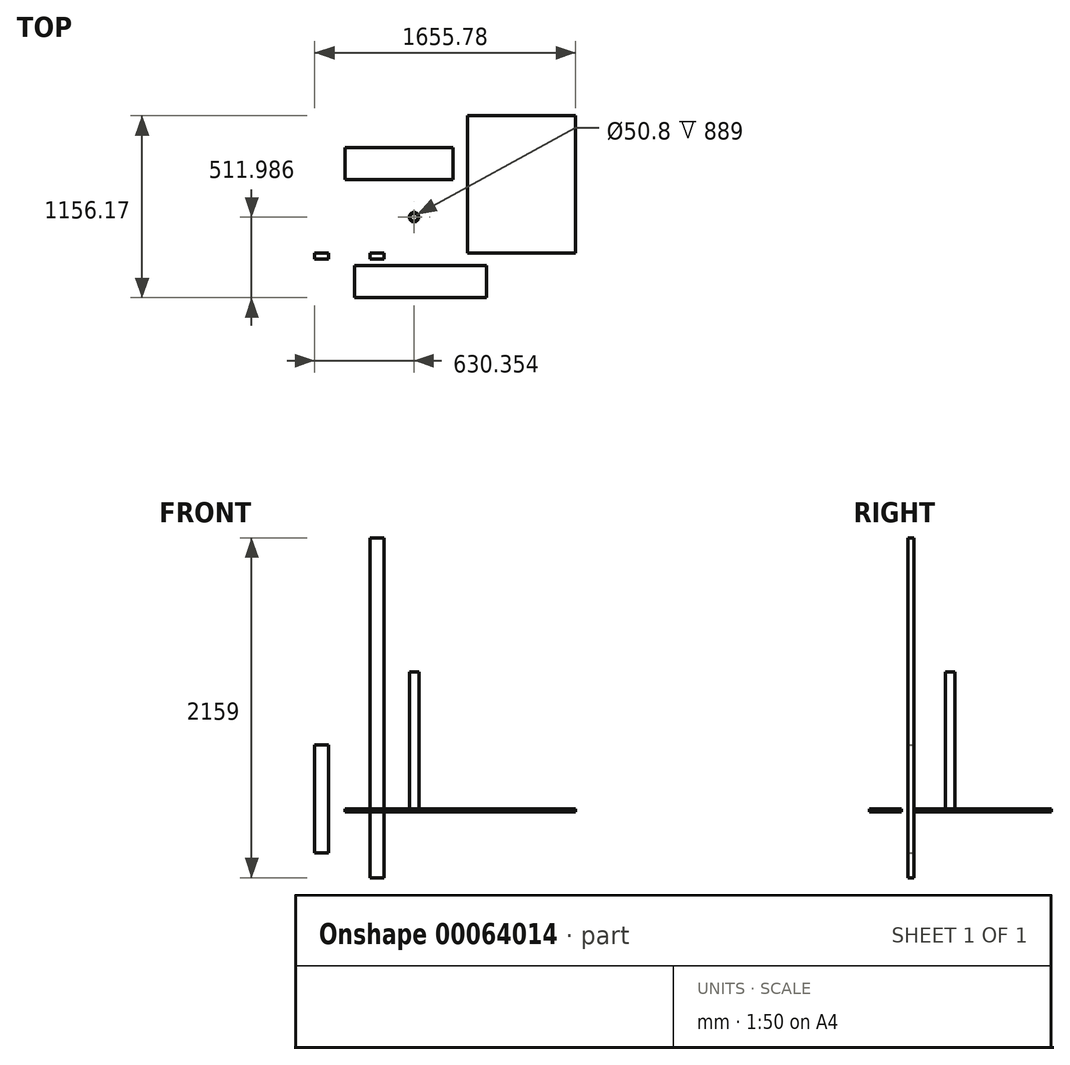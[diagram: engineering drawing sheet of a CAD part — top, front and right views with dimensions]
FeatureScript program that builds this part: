
annotation { "Feature Type Name" : "Feature", "Feature Type Description" : "" }
export const myFeature = defineFeature(function(context is Context, id is Id, definition is map)
    precondition{}
    {
        {
            var Q0;
            Q0=qCreatedBy(makeId("Front.planeOp"),FACE);
            var sketch = newSketch(context, id + "F0", { "sketchPlane" : qUnion([Q0])});
            skLineSegment(sketch, "E0.bottom", {"start": v(-46.7, 1742.14) * mm, "end": v(42.2, 1742.14) * mm});
            skLineSegment(sketch, "E0.top", {"start": v(-46.7, -416.86) * mm, "end": v(42.2, -416.86) * mm});
            skLineSegment(sketch, "E0.left", {"start": v(-46.7, 1742.14) * mm, "end": v(-46.7, -416.86) * mm});
            skLineSegment(sketch, "E0.right", {"start": v(42.2, 1742.14) * mm, "end": v(42.2, -416.86) * mm});
            skSolve(sketch);
        }
        {
            var Q0;
            Q0 = qSketchRegion(id + "F0", true);
            extrude(context, id + "F1", {"entities" : qUnion([Q0]), "depth" : 38.1 * mm});
        }
        {
            var Q0;
            Q0=qCreatedBy(makeId("Front.planeOp"),FACE);
            var sketch = newSketch(context, id + "F2", { "sketchPlane" : qUnion([Q0])});
            skLineSegment(sketch, "E1.bottom", {"start": v(-397.5, 426.42) * mm, "end": v(-308.6, 426.42) * mm});
            skLineSegment(sketch, "E1.top", {"start": v(-397.5, -259.38) * mm, "end": v(-308.6, -259.38) * mm});
            skLineSegment(sketch, "E1.left", {"start": v(-397.5, 426.42) * mm, "end": v(-397.5, -259.38) * mm});
            skLineSegment(sketch, "E1.right", {"start": v(-308.6, 426.42) * mm, "end": v(-308.6, -259.38) * mm});
            skSolve(sketch);
        }
        {
            var Q0;
            Q0 = qSketchRegion(id + "F2", true);
            extrude(context, id + "F3", {"entities" : qUnion([Q0]), "depth" : 38.1 * mm});
        }
        {
            var Q0;
            Q0=qCreatedBy(makeId("Top.planeOp"),FACE);
            var sketch = newSketch(context, id + "F4", { "sketchPlane" : qUnion([Q0])});
            skLineSegment(sketch, "E2.bottom", {"start": v(572.5, 0) * mm, "end": v(1258.3, 0) * mm});
            skLineSegment(sketch, "E2.top", {"start": v(572.5, 873.76) * mm, "end": v(1258.3, 873.76) * mm});
            skLineSegment(sketch, "E2.left", {"start": v(572.5, 0) * mm, "end": v(572.5, 873.76) * mm});
            skLineSegment(sketch, "E2.right", {"start": v(1258.3, 0) * mm, "end": v(1258.3, 873.76) * mm});
            skSolve(sketch);
        }
        {
            var Q0;
            Q0=makeQuery(id+"F4.imprint","IMPRINT",FACE,{"disambiguationData":[TD([[makeQuery(id+"F4.imprint","IMPRINT",EDGE,{"derivedFrom":sQuery(id+"F4.wireOp",EDGE,"E2.bottom")}),1.0]])]});
            extrude(context, id + "F5", {"entities" : qUnion([Q0]), "depth" : 19.05 * mm});
        }
        {
            var Q0;
            Q0=qCreatedBy(makeId("Top.planeOp"),FACE);
            var sketch = newSketch(context, id + "F6", { "sketchPlane" : qUnion([Q0])});
            skLineSegment(sketch, "E3.bottom", {"start": v(479.03, 469.3) * mm, "end": v(-206.77, 469.3) * mm});
            skLineSegment(sketch, "E3.top", {"start": v(479.03, 672.5) * mm, "end": v(-206.77, 672.5) * mm});
            skLineSegment(sketch, "E3.left", {"start": v(479.03, 469.3) * mm, "end": v(479.03, 672.5) * mm});
            skLineSegment(sketch, "E3.right", {"start": v(-206.77, 469.3) * mm, "end": v(-206.77, 672.5) * mm});
            skSolve(sketch);
        }
        {
            var Q0;
            Q0=makeQuery(id+"F6.imprint","IMPRINT",FACE,{"disambiguationData":[TD([[makeQuery(id+"F6.imprint","IMPRINT",EDGE,{"derivedFrom":sQuery(id+"F6.wireOp",EDGE,"E3.bottom")}),-1.0]])]});
            extrude(context, id + "F7", {"entities" : qUnion([Q0]), "depth" : 19.05 * mm});
        }
        {
            var Q0;
            Q0=qCreatedBy(makeId("Top.planeOp"),FACE);
            var sketch = newSketch(context, id + "F8", { "sketchPlane" : qUnion([Q0])});
            skLineSegment(sketch, "E4.bottom", {"start": v(692.25, -79.2) * mm, "end": v(-143.41, -79.2) * mm});
            skLineSegment(sketch, "E4.top", {"start": v(692.25, -282.4) * mm, "end": v(-143.41, -282.4) * mm});
            skLineSegment(sketch, "E4.left", {"start": v(692.25, -79.2) * mm, "end": v(692.25, -282.4) * mm});
            skLineSegment(sketch, "E4.right", {"start": v(-143.41, -79.2) * mm, "end": v(-143.41, -282.4) * mm});
            skSolve(sketch);
        }
        {
            var Q0;
            Q0 = qSketchRegion(id + "F8", true);
            extrude(context, id + "F9", {"entities" : qUnion([Q0]), "depth" : 19.05 * mm});
        }
        {
            var Q0;
            Q0=qCreatedBy(makeId("Top.planeOp"),FACE);
            var sketch = newSketch(context, id + "F10", { "sketchPlane" : qUnion([Q0])});
            skCircle(sketch, "E5", {"center": v(232.86, 229.58) * mm, "radius": 25.4 * mm});
            skCircle(sketch, "E6", {"center": v(232.86, 229.58) * mm, "radius": 30.16 * mm});
            skSolve(sketch);
        }
        {
            var Q0;
            Q0 = qSketchRegion(id + "F10", true);
            extrude(context, id + "F11", {"entities" : qUnion([Q0]), "depth" : 889 * mm});
        }
    });
